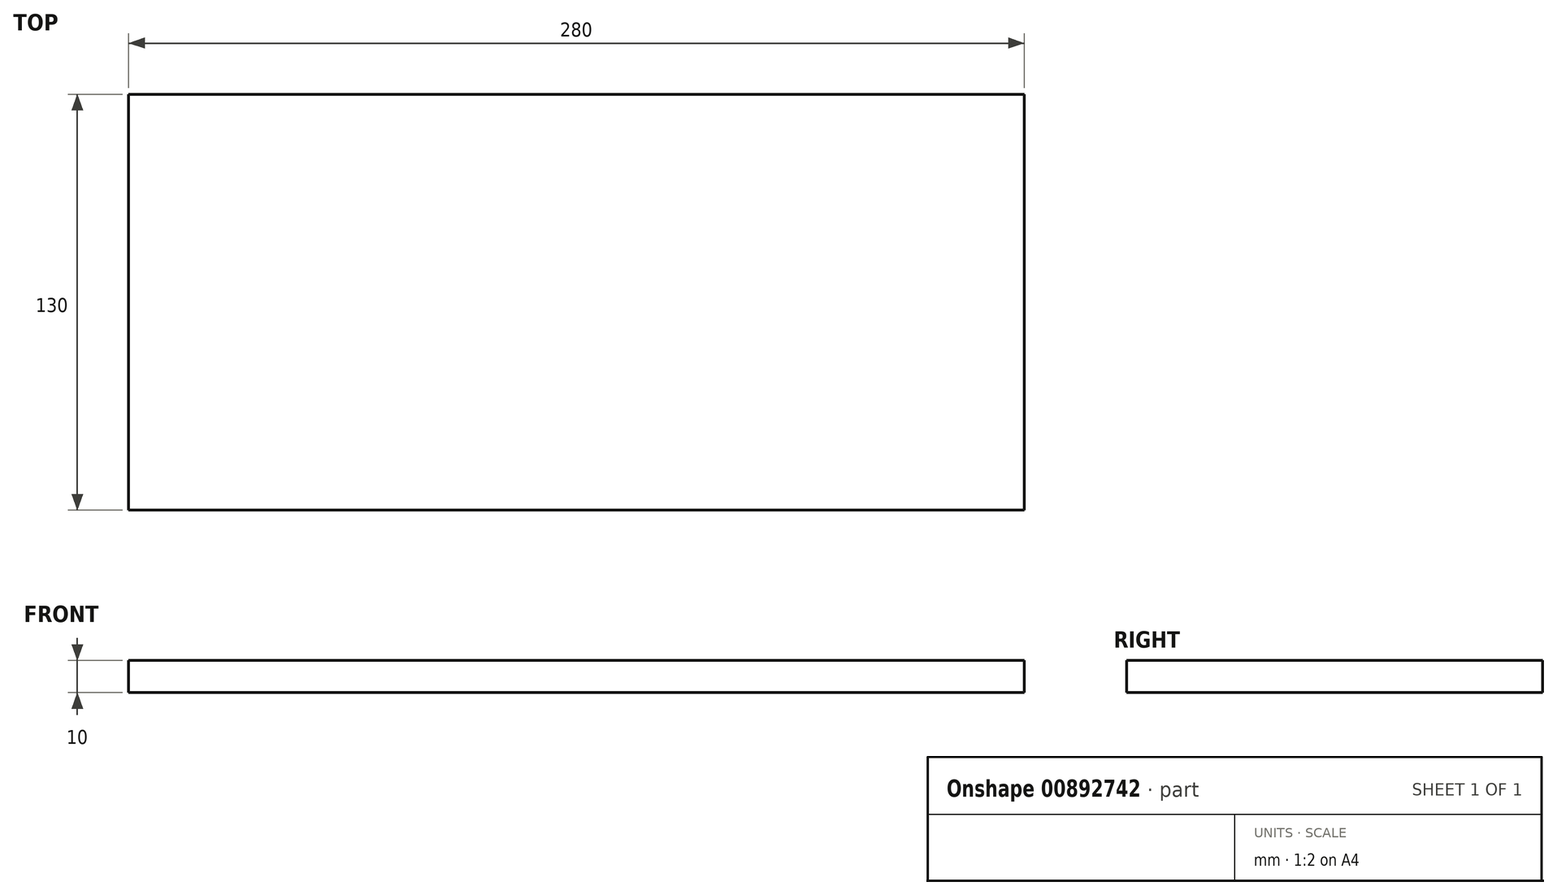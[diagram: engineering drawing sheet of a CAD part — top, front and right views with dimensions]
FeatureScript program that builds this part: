
annotation { "Feature Type Name" : "Feature", "Feature Type Description" : "" }
export const myFeature = defineFeature(function(context is Context, id is Id, definition is map)
    precondition{}
    {
        {
            var Q0;
            Q0=qCreatedBy(makeId("Top.planeOp"),FACE);
            var sketch = newSketch(context, id + "F0", { "sketchPlane" : qUnion([Q0])});
            skLineSegment(sketch, "E0.bottom", {"start": v(140, 65) * mm, "end": v(-140, 65) * mm});
            skLineSegment(sketch, "E0.top", {"start": v(140, -65) * mm, "end": v(-140, -65) * mm});
            skLineSegment(sketch, "E0.left", {"start": v(140, 65) * mm, "end": v(140, -65) * mm});
            skLineSegment(sketch, "E0.right", {"start": v(-140, 65) * mm, "end": v(-140, -65) * mm});
            skPoint(sketch, "E0.middle", {"position": v(0, 0) * mm});
            skSolve(sketch);
        }
        {
            var Q0;
            Q0 = qSketchRegion(id + "F0", true);
            extrude(context, id + "F1", {"entities" : qUnion([Q0]), "depth" : 10 * mm, "offsetDistance" : 25 * mm});
        }
    });
